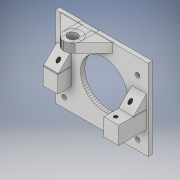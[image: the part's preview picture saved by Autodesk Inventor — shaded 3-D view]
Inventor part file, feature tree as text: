
AUTODESK INVENTOR PART (.ipt)
format: ipt  version: 2017 (Build 210142000, 142)  size: 718,336 bytes
history: native  units: in
note: dims shown in document units (in); Inventor stores cm internally (conversion verified against a paired STEP export)
features: extrude x2, sketch x2, projected_geometry x2, imported_body x1
ambient origin geometry x8: Origin, YZ Plane, XZ Plane, XY Plane, X Axis, Y Axis, Z Axis, Center Point
bodies: Solid1 (feature_tree)
feature tree (7):
  extrude  "Extrusion1"  Depth=0.3937in TaperAngle=0.0deg
  extrude  "Extrusion2"  Depth=0.3937in
  sketch  "Sketch1"  dims[d0=0.252in d1=0.3937in d2=0.0in]
  projected_geometry  "Projected Loop1"
  projected_geometry  "Projected Loop2"
  sketch  "Sketch3"  dims[d6=0.125in d7=0.125in d8=0.125in d9=0.125in d10=0.3937in d11=0.0in]
  imported_body  "Base1"
